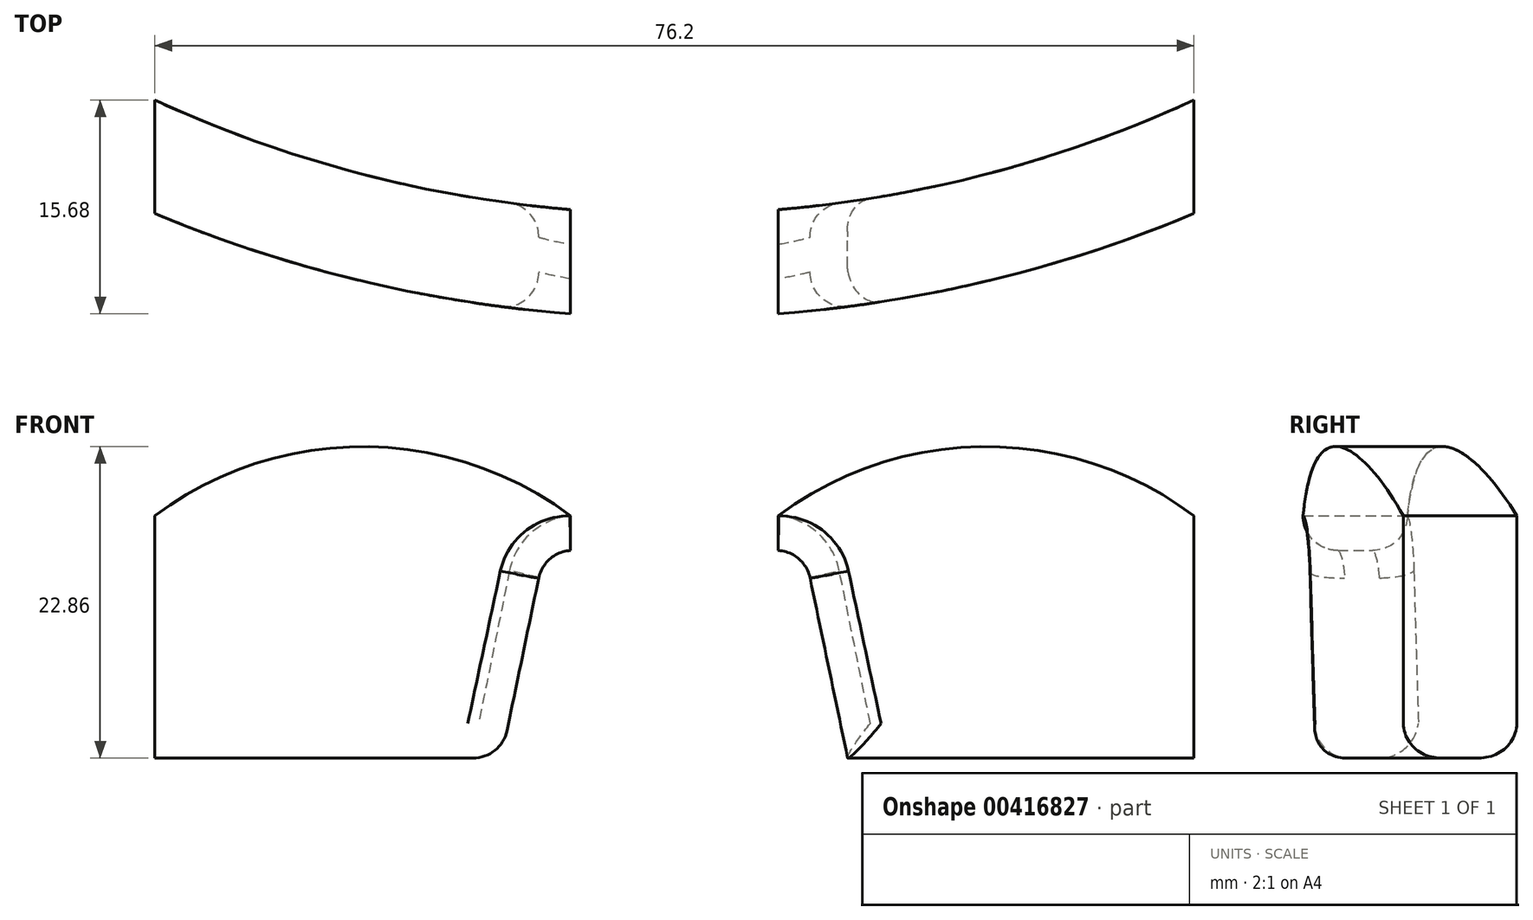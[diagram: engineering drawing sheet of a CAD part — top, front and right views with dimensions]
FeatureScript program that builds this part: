
annotation { "Feature Type Name" : "Feature", "Feature Type Description" : "" }
export const myFeature = defineFeature(function(context is Context, id is Id, definition is map)
    precondition{}
    {
        {
            var Q0;
            Q0=qCreatedBy(makeId("Top.planeOp"),FACE);
            var sketch = newSketch(context, id + "F0", { "sketchPlane" : qUnion([Q0])});
            skArc(sketch, "E0", {"start": v(-70.48, -11.41) * mm, "mid": v(0, -41.03) * mm, "end": v(70.49, -11.41) * mm});
            skLineSegment(sketch, "E1", {"start": v(0, 0) * mm, "end": v(0, 211.05) * mm, "construction": true});
            skArc(sketch, "E2", {"start": v(-70.48, 0) * mm, "mid": v(0, -33.4) * mm, "end": v(70.48, 0) * mm});
            skLineSegment(sketch, "E3", {"start": v(-70.49, 0) * mm, "end": v(-70.49, -11.41) * mm});
            skLineSegment(sketch, "E4", {"start": v(70.48, 0) * mm, "end": v(70.48, -11.41) * mm});
            skLineSegment(sketch, "E5", {"start": v(70.48, 0) * mm, "end": v(-70.48, 0) * mm, "construction": true});
            skSolve(sketch);
        }
        {
            var Q0;
            Q0=makeQuery(id+"F0.imprint","IMPRINT",FACE,{"disambiguationData":[TD([[makeQuery(id+"F0.imprint","IMPRINT",EDGE,{"derivedFrom":sQuery(id+"F0.wireOp",EDGE,"E0")}),1.0]])]});
            extrude(context, id + "F1", {"entities" : qUnion([Q0]), "depth" : 81.28 * mm, "offsetDistance" : 25.4 * mm});
        }
        {
            var Q0;
            Q0=qCreatedBy(makeId("Front.planeOp"),FACE);
            var sketch = newSketch(context, id + "F2", { "sketchPlane" : qUnion([Q0])});
            skLineSegment(sketch, "E6.bottom", {"start": v(-50.8, 73.66) * mm, "end": v(50.8, 73.66) * mm});
            skLineSegment(sketch, "E6.left", {"start": v(-63.5, 60.96) * mm, "end": v(-63.5, 21.59) * mm});
            skLineSegment(sketch, "E6.right", {"start": v(63.5, 60.96) * mm, "end": v(63.5, 21.6) * mm});
            skPoint(sketch, "E7.visualSharp", {"position": v(-63.5, 73.66) * mm});
            skArc(sketch, "E7.filletArc", {"start": v(-50.8, 73.66) * mm, "mid": v(-59.78, 69.94) * mm, "end": v(-63.5, 60.96) * mm});
            skPoint(sketch, "E8.visualSharp", {"position": v(63.5, 73.66) * mm});
            skArc(sketch, "E8.filletArc", {"start": v(63.5, 60.96) * mm, "mid": v(59.78, 69.94) * mm, "end": v(50.8, 73.66) * mm});
            skLineSegment(sketch, "E9", {"start": v(57.15, 15.24) * mm, "end": v(19.1, 15.24) * mm});
            skLineSegment(sketch, "E10", {"start": v(-19.1, 15.24) * mm, "end": v(-57.15, 15.24) * mm});
            skLineSegment(sketch, "E11", {"start": v(0, 0) * mm, "end": v(0, 74.9) * mm, "construction": true});
            skLineSegment(sketch, "E12", {"start": v(-16.71, 16.91) * mm, "end": v(-15.74, 19.58) * mm});
            skLineSegment(sketch, "E13", {"start": v(-3.8, 27.94) * mm, "end": v(3.8, 27.94) * mm});
            skLineSegment(sketch, "E14", {"start": v(15.74, 19.58) * mm, "end": v(16.71, 16.91) * mm});
            skPoint(sketch, "E15.visualSharp", {"position": v(-12.7, 27.94) * mm});
            skArc(sketch, "E15.filletArc", {"start": v(-3.8, 27.94) * mm, "mid": v(-11.1, 25.64) * mm, "end": v(-15.74, 19.58) * mm});
            skPoint(sketch, "E16.visualSharp", {"position": v(12.7, 27.94) * mm});
            skArc(sketch, "E16.filletArc", {"start": v(15.74, 19.58) * mm, "mid": v(11.1, 25.64) * mm, "end": v(3.8, 27.94) * mm});
            skPoint(sketch, "E17.visualSharp", {"position": v(-17.32, 15.24) * mm});
            skArc(sketch, "E17.filletArc", {"start": v(-19.1, 15.24) * mm, "mid": v(-17.64, 15.7) * mm, "end": v(-16.71, 16.91) * mm});
            skPoint(sketch, "E18.visualSharp", {"position": v(17.32, 15.24) * mm});
            skArc(sketch, "E18.filletArc", {"start": v(16.71, 16.91) * mm, "mid": v(17.64, 15.7) * mm, "end": v(19.1, 15.24) * mm});
            skPoint(sketch, "E19.visualSharp", {"position": v(-63.5, 15.24) * mm});
            skArc(sketch, "E19.filletArc", {"start": v(-63.5, 21.59) * mm, "mid": v(-61.64, 17.1) * mm, "end": v(-57.15, 15.24) * mm});
            skPoint(sketch, "E20.visualSharp", {"position": v(63.5, 15.24) * mm});
            skArc(sketch, "E20.filletArc", {"start": v(57.15, 15.24) * mm, "mid": v(61.64, 17.1) * mm, "end": v(63.5, 21.6) * mm});
            skLineSegment(sketch, "E21", {"start": v(19.1, 15.24) * mm, "end": v(-19.1, 15.24) * mm});
            skLineSegment(sketch, "E22", {"start": v(88.9, 0) * mm, "end": v(88.9, 83.82) * mm});
            skLineSegment(sketch, "E23", {"start": v(-88.9, 83.82) * mm, "end": v(-88.9, 0) * mm});
            skLineSegment(sketch, "E24", {"start": v(-88.9, 0) * mm, "end": v(88.9, 0) * mm});
            skLineSegment(sketch, "E25", {"start": v(88.9, 83.82) * mm, "end": v(-88.9, 83.82) * mm});
            skSolve(sketch);
        }
        {
            var Q0;
            Q0=qCreatedBy(makeId("Top.planeOp"),FACE);
            var sketch = newSketch(context, id + "F3", { "sketchPlane" : qUnion([Q0])});
            skCircle(sketch, "E26", {"center": v(0, 57.15) * mm, "radius": 98.68 * mm});
            skCircle(sketch, "E27", {"center": v(0, 57.15) * mm, "radius": 97.4 * mm});
            skLineSegment(sketch, "E28", {"start": v(-89.52, 0) * mm, "end": v(0, 0) * mm, "construction": true});
            skLineSegment(sketch, "E29", {"start": v(-71.12, 0) * mm, "end": v(-71.12, -9.41) * mm});
            skLineSegment(sketch, "E30", {"start": v(-63.5, 0) * mm, "end": v(-63.5, -16.72) * mm});
            skLineSegment(sketch, "E31.MirrorCS", {"start": v(71.12, 0) * mm, "end": v(71.12, -9.41) * mm});
            skLineSegment(sketch, "E32.MirrorCS", {"start": v(89.52, 0) * mm, "end": v(0, 0) * mm, "construction": true});
            skLineSegment(sketch, "E33.MirrorCS", {"start": v(63.5, 0) * mm, "end": v(63.5, -16.72) * mm});
            skLineSegment(sketch, "E34", {"start": v(-71.12, 0) * mm, "end": v(-63.5, 0) * mm});
            skLineSegment(sketch, "E35", {"start": v(63.5, 0) * mm, "end": v(71.12, 0) * mm});
            skSolve(sketch);
        }
        {
            var Q0;
            Q0=makeQuery(id+"F1.opExtrude","CAP_EDGE",EDGE,{"disambiguationData":[OSD([sQuery(id+"F0.wireOp",EDGE,"E3")])],"isStart":false});
            var Q1;
            Q1=makeQuery(id+"F1.opExtrude","CAP_EDGE",EDGE,{"disambiguationData":[OSD([sQuery(id+"F0.wireOp",EDGE,"E4")])],"isStart":false});
            var Q2;
            Q2=makeQuery(id+"F1.opExtrude","CAP_EDGE",EDGE,{"disambiguationData":[OSD([sQuery(id+"F0.wireOp",EDGE,"E3")])],"isStart":true});
            var Q3;
            Q3=makeQuery(id+"F1.opExtrude","CAP_EDGE",EDGE,{"disambiguationData":[OSD([sQuery(id+"F0.wireOp",EDGE,"E4")])],"isStart":true});
            fillet(context, id + "F4", {"entities" : qUnion([Q0, Q1, Q2, Q3]), "radius" : 25.4 * mm, "tangentPropagation" : true, "allowEdgeOverflow" : false});
        }
        {
            var Q0;
            Q0=makeQuery(id+"F2.imprint","IMPRINT",FACE,{"disambiguationData":[TD([[makeQuery(id+"F2.imprint","IMPRINT",EDGE,{"derivedFrom":sQuery(id+"F2.wireOp",EDGE,"E6.bottom")}),1.0]])]});
            var sketch = newSketch(context, id + "F5", { "sketchPlane" : qUnion([Q0])});
            skLineSegment(sketch, "E36", {"start": v(-12.7, 0) * mm, "end": v(-9.53, 15.24) * mm});
            skLineSegment(sketch, "E37", {"start": v(-9.53, 15.24) * mm, "end": v(9.52, 15.24) * mm});
            skLineSegment(sketch, "E38", {"start": v(9.52, 15.24) * mm, "end": v(12.7, 0) * mm});
            skLineSegment(sketch, "E39", {"start": v(12.7, 0) * mm, "end": v(-12.7, 0) * mm});
            skSolve(sketch);
        }
        {
            var Q0;
            Q0=qSketchRegion(id+"F5",true);
            extrude(context, id + "F6", {"entities" : qUnion([Q0]), "operationType" : NewBodyOperationType.REMOVE, "endBound" : BoundingType.THROUGH_ALL, "depth" : 25.4 * mm, "offsetDistance" : 25.4 * mm});
        }
        {
            var Q0;
            Q0=makeQuery(id+"F6.boolean.opBoolean","COPY",EDGE,{"derivedFrom":makeQuery(id+"F6.opExtrude","SWEPT_EDGE",EDGE,{"disambiguationData":[OSD([sQuery(id+"F2.wireOp",EDGE,"E21"),sQuery(id+"F5.wireOp",EDGE,"E36"),sQuery(id+"F5.wireOp",EDGE,"E37")])]})});
            var Q1;
            Q1=makeQuery(id+"F6.boolean.opBoolean","COPY",EDGE,{"derivedFrom":makeQuery(id+"F6.opExtrude","SWEPT_EDGE",EDGE,{"disambiguationData":[OSD([sQuery(id+"F2.wireOp",EDGE,"E21"),sQuery(id+"F5.wireOp",EDGE,"E37"),sQuery(id+"F5.wireOp",EDGE,"E38")])]})});
            var Q2;
            Q2=makeQuery(id+"F6.boolean.opBoolean","COPY",EDGE,{"derivedFrom":makeQuery(id+"F6.opExtrude","SWEPT_EDGE",EDGE,{"disambiguationData":[OSD([sQuery(id+"F2.wireOp",EDGE,"E24"),sQuery(id+"F5.wireOp",EDGE,"E38"),sQuery(id+"F5.wireOp",EDGE,"E39")])]})});
            var Q3;
            Q3=makeQuery(id+"F6.boolean.opBoolean","COPY",EDGE,{"derivedFrom":makeQuery(id+"F6.opExtrude","SWEPT_EDGE",EDGE,{"disambiguationData":[OSD([sQuery(id+"F2.wireOp",EDGE,"E24"),sQuery(id+"F5.wireOp",EDGE,"E36"),sQuery(id+"F5.wireOp",EDGE,"E39")])]})});
            fillet(context, id + "F7", {"entities" : qUnion([Q0, Q1, Q2, Q3]), "radius" : 2.54 * mm, "tangentPropagation" : true, "allowEdgeOverflow" : false});
        }
        {
            var Q0;
            Q0=makeQuery(id+"F4.opFillet","BLEND_EDGE",EDGE,{"blendedFrom":[makeQuery(id+"F1.opExtrude","CAP_EDGE",EDGE,{"disambiguationData":[OSD([sQuery(id+"F0.wireOp",EDGE,"E4")])],"isStart":false}),makeQuery(id+"F1.opExtrude","SWEPT_FACE",FACE,{"disambiguationData":[OSD([sQuery(id+"F0.wireOp",EDGE,"E0")])]})],"blendedInto":[makeQuery(id+"F1.opExtrude","SWEPT_FACE",FACE,{"disambiguationData":[OSD([sQuery(id+"F0.wireOp",EDGE,"E0")])]})]});
            var Q1;
            Q1=makeQuery(id+"F1.opExtrude","CAP_EDGE",EDGE,{"disambiguationData":[OSD([sQuery(id+"F0.wireOp",EDGE,"E2")])],"isStart":false});
            fillet(context, id + "F8", {"entities" : qUnion([Q0, Q1]), "radius" : 2.54 * mm, "tangentPropagation" : true, "defaultsChanged" : false, "vertexSettings" : [], "allowEdgeOverflow" : false});
        }
        {
            var Q0;
            Q0=qCreatedBy(makeId("Front.planeOp"),FACE);
            var sketch = newSketch(context, id + "F9", { "sketchPlane" : qUnion([Q0])});
            skLineSegment(sketch, "E40.bottom", {"start": v(-45.72, 30.48) * mm, "end": v(45.72, 30.48) * mm});
            skLineSegment(sketch, "E40.top", {"start": v(-8.38, 17.78) * mm, "end": v(8.38, 17.78) * mm});
            skLineSegment(sketch, "E40.left", {"start": v(-50.8, 25.4) * mm, "end": v(-50.8, 17.78) * mm});
            skLineSegment(sketch, "E40.right", {"start": v(50.8, 25.4) * mm, "end": v(50.8, 17.78) * mm});
            skLineSegment(sketch, "E41", {"start": v(0, 0) * mm, "end": v(0, 124.67) * mm, "construction": true});
            skLineSegment(sketch, "E42", {"start": v(-14.54, 12.97) * mm, "end": v(-16.5, 5.08) * mm});
            skLineSegment(sketch, "E43", {"start": v(-16.5, 5.08) * mm, "end": v(-45.72, 5.08) * mm});
            skLineSegment(sketch, "E44", {"start": v(-50.8, 10.16) * mm, "end": v(-50.8, 17.78) * mm});
            skPoint(sketch, "E45.newPointB", {"position": v(-50.8, 17.78) * mm});
            skArc(sketch, "E45.filletArc", {"start": v(-8.38, 17.78) * mm, "mid": v(-12.3, 16.43) * mm, "end": v(-14.54, 12.97) * mm});
            skLineSegment(sketch, "E46.MirrorCS", {"start": v(16.5, 5.08) * mm, "end": v(45.72, 5.08) * mm});
            skLineSegment(sketch, "E47.MirrorCS", {"start": v(14.54, 12.97) * mm, "end": v(16.5, 5.08) * mm});
            skArc(sketch, "E48.MirrorCS", {"start": v(8.38, 17.78) * mm, "mid": v(12.3, 16.43) * mm, "end": v(14.54, 12.97) * mm});
            skLineSegment(sketch, "E49.MirrorCS", {"start": v(50.8, 10.16) * mm, "end": v(50.8, 17.78) * mm});
            skPoint(sketch, "E50.visualSharp", {"position": v(-50.8, 30.48) * mm});
            skArc(sketch, "E50.filletArc", {"start": v(-45.72, 30.48) * mm, "mid": v(-49.31, 29) * mm, "end": v(-50.8, 25.4) * mm});
            skPoint(sketch, "E51.visualSharp", {"position": v(50.8, 30.48) * mm});
            skArc(sketch, "E51.filletArc", {"start": v(50.8, 25.4) * mm, "mid": v(49.31, 29) * mm, "end": v(45.72, 30.48) * mm});
            skPoint(sketch, "E52.visualSharp", {"position": v(50.8, 5.08) * mm});
            skArc(sketch, "E52.filletArc", {"start": v(45.72, 5.08) * mm, "mid": v(49.31, 6.57) * mm, "end": v(50.8, 10.16) * mm});
            skPoint(sketch, "E53.visualSharp", {"position": v(-50.8, 5.08) * mm});
            skArc(sketch, "E53.filletArc", {"start": v(-50.8, 10.16) * mm, "mid": v(-49.31, 6.57) * mm, "end": v(-45.72, 5.08) * mm});
            skSolve(sketch);
        }
        {
            var Q0;
            Q0=qCreatedBy(makeId("Front.planeOp"),FACE);
            var sketch = newSketch(context, id + "F10", { "sketchPlane" : qUnion([Q0])});
            skLineSegment(sketch, "E54.bottom", {"start": v(-38.1, 0) * mm, "end": v(38.1, 0) * mm});
            skLineSegment(sketch, "E54.top", {"start": v(-7.62, 17.78) * mm, "end": v(7.62, 17.78) * mm});
            skLineSegment(sketch, "E54.left", {"start": v(-38.1, 0) * mm, "end": v(-38.1, 17.78) * mm});
            skLineSegment(sketch, "E54.right", {"start": v(38.1, 0) * mm, "end": v(38.1, 17.78) * mm});
            skArc(sketch, "E55", {"start": v(-7.62, 17.78) * mm, "mid": v(-22.86, 22.86) * mm, "end": v(-38.1, 17.78) * mm});
            skArc(sketch, "E56", {"start": v(38.1, 17.78) * mm, "mid": v(22.86, 22.86) * mm, "end": v(7.62, 17.78) * mm});
            skLineSegment(sketch, "E57", {"start": v(-7.62, 17.78) * mm, "end": v(-7.62, 0) * mm});
            skLineSegment(sketch, "E58", {"start": v(7.62, 17.78) * mm, "end": v(7.62, 0) * mm});
            skLineSegment(sketch, "E59", {"start": v(-38.1, 0) * mm, "end": v(-76.2, 0) * mm});
            skLineSegment(sketch, "E60", {"start": v(-76.2, 0) * mm, "end": v(-76.2, 88.9) * mm});
            skLineSegment(sketch, "E61", {"start": v(-76.2, 88.9) * mm, "end": v(76.2, 88.9) * mm});
            skLineSegment(sketch, "E62", {"start": v(76.2, 88.9) * mm, "end": v(76.2, 0) * mm});
            skLineSegment(sketch, "E63", {"start": v(76.2, 0) * mm, "end": v(38.1, 0) * mm});
            skSolve(sketch);
        }
        {
            var Q0;
            Q0=makeQuery(id+"F10.imprint","IMPRINT",FACE,{"disambiguationData":[TD([[makeQuery(id+"F10.imprint","IMPRINT",EDGE,{"derivedFrom":sQuery(id+"F10.wireOp",EDGE,"E54.top")}),-1.0]])]});
            var Q1;
            Q1=makeQuery(id+"F10.imprint","IMPRINT",FACE,{"disambiguationData":[TD([[makeQuery(id+"F10.imprint","IMPRINT",EDGE,{"derivedFrom":sQuery(id+"F10.wireOp",EDGE,"E54.top")}),1.0]])]});
            extrude(context, id + "F11", {"entities" : qUnion([Q0, Q1]), "operationType" : NewBodyOperationType.REMOVE, "endBound" : BoundingType.THROUGH_ALL, "depth" : 25.4 * mm, "offsetDistance" : 25.4 * mm});
        }
    });
